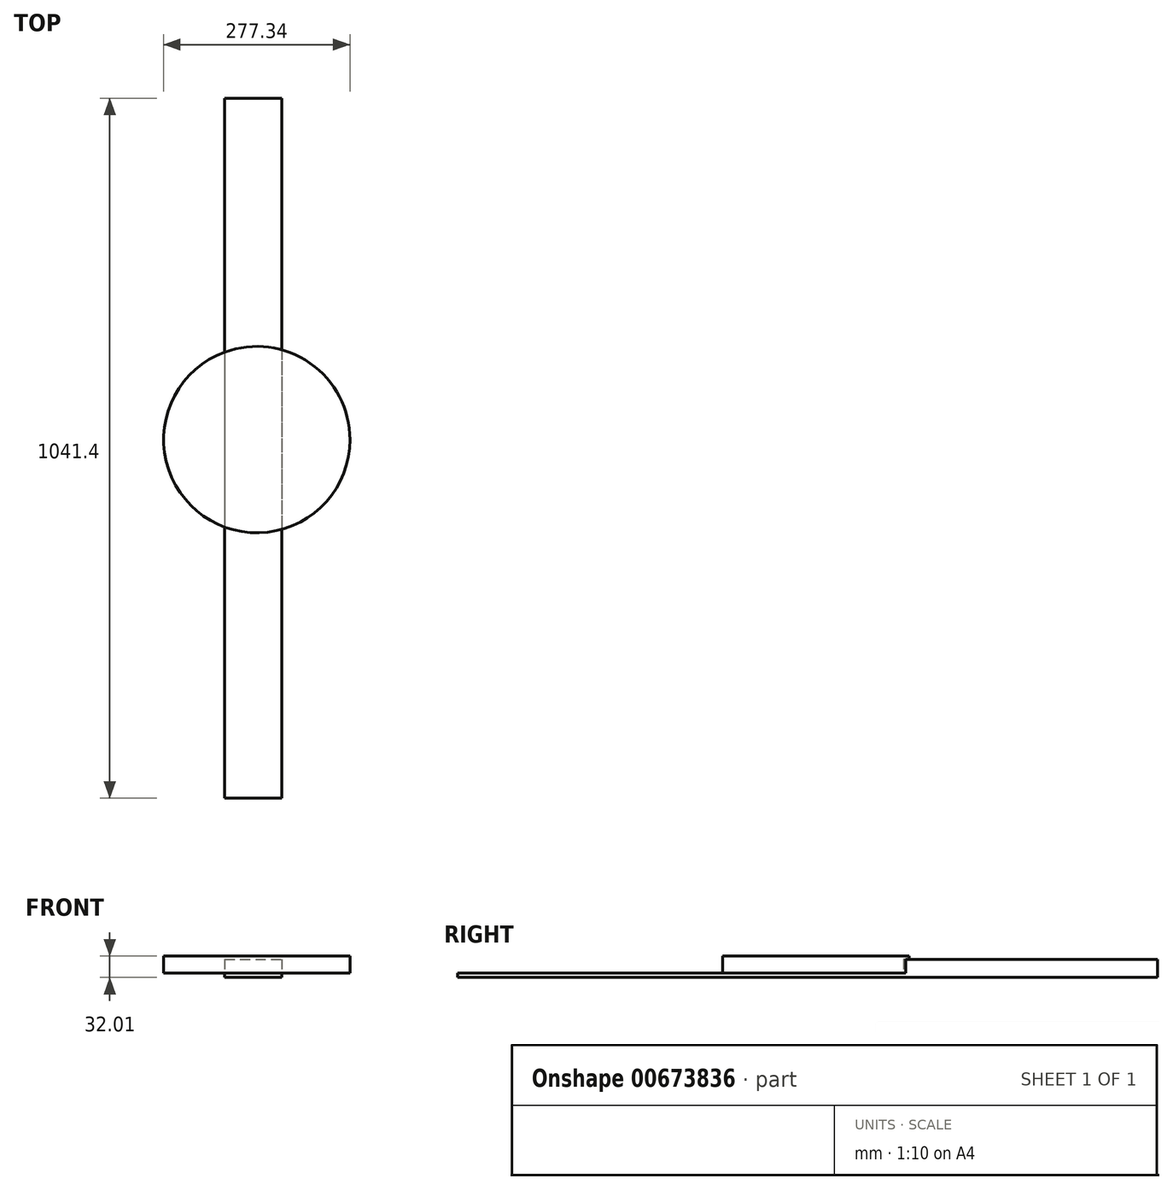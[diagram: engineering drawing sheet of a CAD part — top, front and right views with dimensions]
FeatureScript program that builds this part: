
annotation { "Feature Type Name" : "Feature", "Feature Type Description" : "" }
export const myFeature = defineFeature(function(context is Context, id is Id, definition is map)
    precondition{}
    {
        {
            var Q0;
            Q0=qCreatedBy(makeId("Top.planeOp"),FACE);
            var sketch = newSketch(context, id + "F0", { "sketchPlane" : qUnion([Q0])});
            skCircle(sketch, "E0", {"center": v(0, 0) * mm, "radius": 138.67 * mm});
            skSolve(sketch);
        }
        {
            var Q0;
            Q0 = qSketchRegion(id + "F0", true);
            var Q1;
            Q1=makeQuery(id+"F0.imprint","IMPRINT",FACE,{"disambiguationData":[TD([[makeQuery(id+"F0.imprint","IMPRINT",EDGE,{"derivedFrom":sQuery(id+"F0.wireOp",EDGE,"E0")}),1.0]])]});
            extrude(context, id + "F1", {"entities" : qUnion([Q0, Q1]), "depth" : 25.4 * mm, "offsetDistance" : 25.4 * mm});
        }
        {
            var Q0;
            Q0=qCreatedBy(makeId("Front.planeOp"),FACE);
            var sketch = newSketch(context, id + "F2", { "sketchPlane" : qUnion([Q0])});
            skLineSegment(sketch, "E1.bottom", {"start": v(-47.82, 20.4) * mm, "end": v(37.24, 20.4) * mm});
            skLineSegment(sketch, "E1.top", {"start": v(-47.82, -6.61) * mm, "end": v(37.24, -6.61) * mm});
            skLineSegment(sketch, "E1.left", {"start": v(-47.82, 20.4) * mm, "end": v(-47.82, -6.61) * mm});
            skLineSegment(sketch, "E1.right", {"start": v(37.24, 20.4) * mm, "end": v(37.24, -6.61) * mm});
            skLineSegment(sketch, "E2.bottom", {"start": v(-153.43, -113.97) * mm, "end": v(76.37, -113.97) * mm});
            skLineSegment(sketch, "E2.top", {"start": v(-153.43, -114.21) * mm, "end": v(76.37, -114.21) * mm});
            skLineSegment(sketch, "E2.left", {"start": v(-153.43, -113.97) * mm, "end": v(-153.43, -114.21) * mm});
            skLineSegment(sketch, "E2.right", {"start": v(76.37, -113.97) * mm, "end": v(76.37, -114.21) * mm});
            skSolve(sketch);
        }
        {
            var Q0;
            Q0=makeQuery(id+"F2.imprint","IMPRINT",FACE,{"disambiguationData":[TD([[makeQuery(id+"F2.imprint","IMPRINT",EDGE,{"derivedFrom":sQuery(id+"F2.wireOp",EDGE,"E1.bottom")}),-1.0]])]});
            extrude(context, id + "F3", {"entities" : qUnion([Q0]), "operationType" : NewBodyOperationType.ADD, "oppositeDirection" : true, "depth" : 508 * mm, "offsetDistance" : 25.4 * mm, "hasSecondDirection" : true, "secondDirectionOppositeDirection" : false, "secondDirectionDepth" : 25.4 * mm});
        }
        {
            var Q0;
            Q0=makeQuery(id+"F3.opExtrude","CAP_FACE",FACE,{"disambiguationData":[OSD([sQuery(id+"F2.wireOp",EDGE,"E1.bottom"),sQuery(id+"F2.wireOp",EDGE,"E1.top"),sQuery(id+"F2.wireOp",EDGE,"E1.left"),sQuery(id+"F2.wireOp",EDGE,"E1.right")])],"isStart":true});
            extrude(context, id + "F4", {"entities" : qUnion([Q0]), "operationType" : NewBodyOperationType.ADD, "depth" : 508 * mm, "offsetDistance" : 25.4 * mm});
        }
    });
